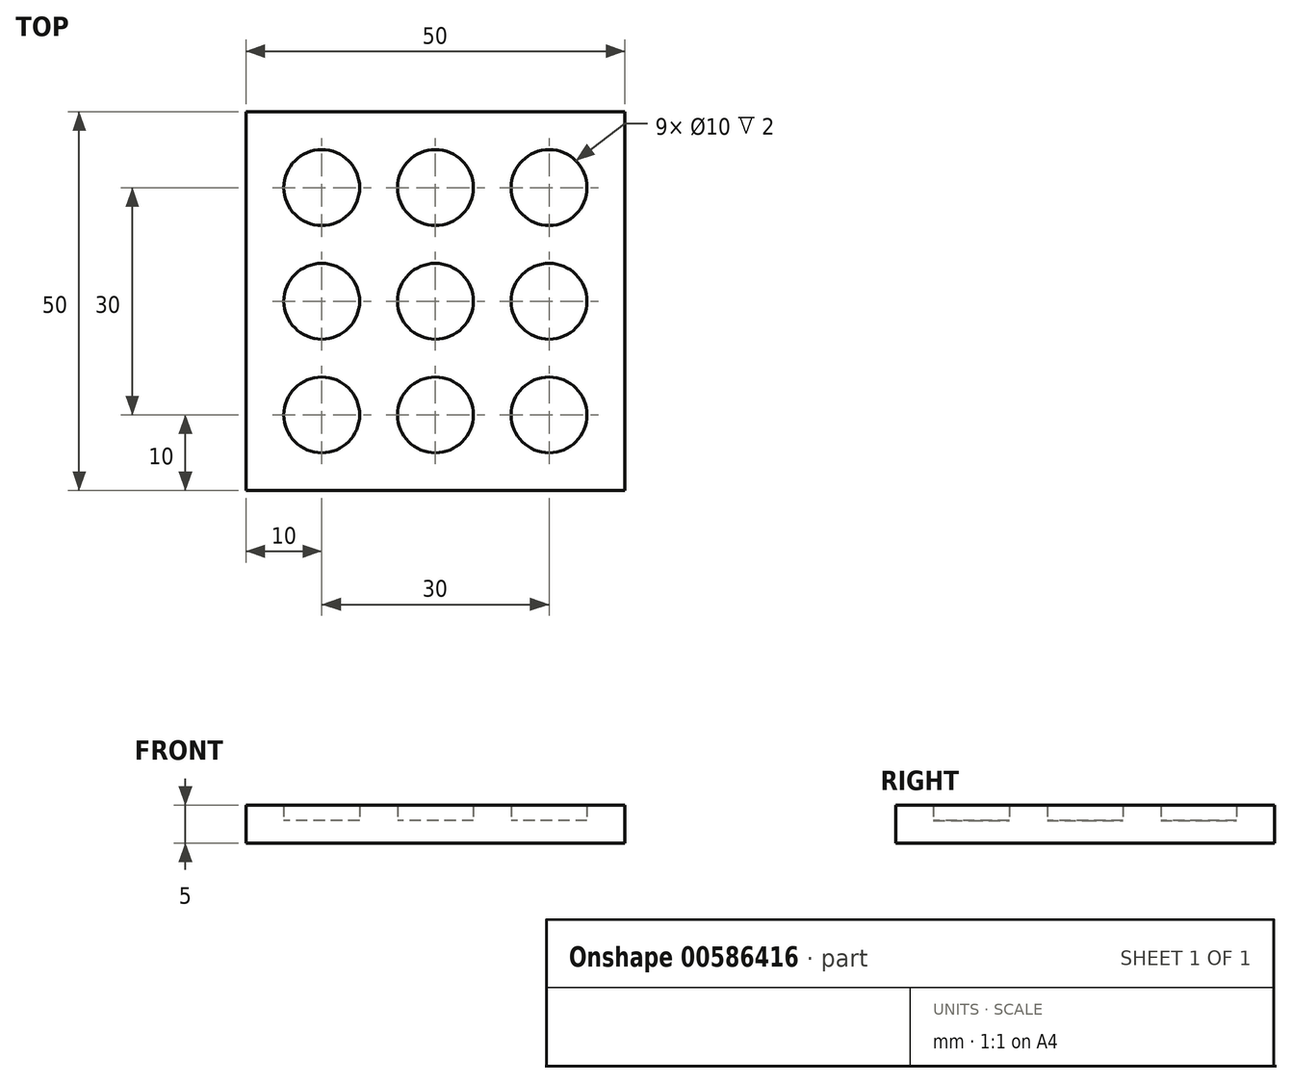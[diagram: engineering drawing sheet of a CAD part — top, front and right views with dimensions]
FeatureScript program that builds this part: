
annotation { "Feature Type Name" : "Feature", "Feature Type Description" : "" }
export const myFeature = defineFeature(function(context is Context, id is Id, definition is map)
    precondition{}
    {
        {
            var Q0;
            Q0=qCreatedBy(makeId("Top.planeOp"),FACE);
            var sketch = newSketch(context, id + "F0", { "sketchPlane" : qUnion([Q0])});
            skLineSegment(sketch, "E0.bottom", {"start": v(25, -25) * mm, "end": v(-25, -25) * mm});
            skLineSegment(sketch, "E0.top", {"start": v(25, 25) * mm, "end": v(-25, 25) * mm});
            skLineSegment(sketch, "E0.left", {"start": v(25, -25) * mm, "end": v(25, 25) * mm});
            skLineSegment(sketch, "E0.right", {"start": v(-25, -25) * mm, "end": v(-25, 25) * mm});
            skPoint(sketch, "E0.middle", {"position": v(0, 0) * mm});
            skCircle(sketch, "E1", {"center": v(-15, 15) * mm, "radius": 5 * mm});
            skCircle(sketch, "E2", {"center": v(0, 15) * mm, "radius": 5 * mm});
            skCircle(sketch, "E3", {"center": v(15, 15) * mm, "radius": 5 * mm});
            skCircle(sketch, "E4", {"center": v(15, -15) * mm, "radius": 5 * mm});
            skCircle(sketch, "E5", {"center": v(0, -15) * mm, "radius": 5 * mm});
            skCircle(sketch, "E6", {"center": v(-15, -15) * mm, "radius": 5 * mm});
            skCircle(sketch, "E7", {"center": v(-15, 0) * mm, "radius": 5 * mm});
            skCircle(sketch, "E8", {"center": v(0, 0) * mm, "radius": 5 * mm});
            skCircle(sketch, "E9", {"center": v(15, 0) * mm, "radius": 5 * mm});
            skSolve(sketch);
        }
        {
            var Q0;
            Q0=makeQuery(id+"F0.imprint","IMPRINT",FACE,{"disambiguationData":[TD([[makeQuery(id+"F0.imprint","IMPRINT",EDGE,{"derivedFrom":sQuery(id+"F0.wireOp",EDGE,"E0.bottom")}),-1.0]])]});
            var Q1;
            Q1=makeQuery(id+"F0.imprint","IMPRINT",FACE,{"disambiguationData":[TD([[makeQuery(id+"F0.imprint","IMPRINT",EDGE,{"derivedFrom":sQuery(id+"F0.wireOp",EDGE,"E1")}),1.0]])]});
            var Q2;
            Q2=makeQuery(id+"F0.imprint","IMPRINT",FACE,{"disambiguationData":[TD([[makeQuery(id+"F0.imprint","IMPRINT",EDGE,{"derivedFrom":sQuery(id+"F0.wireOp",EDGE,"E2")}),1.0]])]});
            var Q3;
            Q3=makeQuery(id+"F0.imprint","IMPRINT",FACE,{"disambiguationData":[TD([[makeQuery(id+"F0.imprint","IMPRINT",EDGE,{"derivedFrom":sQuery(id+"F0.wireOp",EDGE,"E3")}),1.0]])]});
            var Q4;
            Q4=makeQuery(id+"F0.imprint","IMPRINT",FACE,{"disambiguationData":[TD([[makeQuery(id+"F0.imprint","IMPRINT",EDGE,{"derivedFrom":sQuery(id+"F0.wireOp",EDGE,"E9")}),1.0]])]});
            var Q5;
            Q5=makeQuery(id+"F0.imprint","IMPRINT",FACE,{"disambiguationData":[TD([[makeQuery(id+"F0.imprint","IMPRINT",EDGE,{"derivedFrom":sQuery(id+"F0.wireOp",EDGE,"E8")}),1.0]])]});
            var Q6;
            Q6=makeQuery(id+"F0.imprint","IMPRINT",FACE,{"disambiguationData":[TD([[makeQuery(id+"F0.imprint","IMPRINT",EDGE,{"derivedFrom":sQuery(id+"F0.wireOp",EDGE,"E7")}),1.0]])]});
            var Q7;
            Q7=makeQuery(id+"F0.imprint","IMPRINT",FACE,{"disambiguationData":[TD([[makeQuery(id+"F0.imprint","IMPRINT",EDGE,{"derivedFrom":sQuery(id+"F0.wireOp",EDGE,"E6")}),1.0]])]});
            var Q8;
            Q8=makeQuery(id+"F0.imprint","IMPRINT",FACE,{"disambiguationData":[TD([[makeQuery(id+"F0.imprint","IMPRINT",EDGE,{"derivedFrom":sQuery(id+"F0.wireOp",EDGE,"E5")}),1.0]])]});
            var Q9;
            Q9=makeQuery(id+"F0.imprint","IMPRINT",FACE,{"disambiguationData":[TD([[makeQuery(id+"F0.imprint","IMPRINT",EDGE,{"derivedFrom":sQuery(id+"F0.wireOp",EDGE,"E4")}),1.0]])]});
            extrude(context, id + "F1", {"entities" : qUnion([Q0, Q1, Q2, Q3, Q4, Q5, Q6, Q7, Q8, Q9]), "depth" : 3 * mm, "offsetDistance" : 25 * mm});
        }
        {
            var Q0;
            Q0 = qSketchRegion(id + "F0", true);
            extrude(context, id + "F2", {"entities" : qUnion([Q0]), "operationType" : NewBodyOperationType.ADD, "depth" : 5 * mm, "offsetDistance" : 25 * mm});
        }
    });
